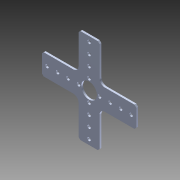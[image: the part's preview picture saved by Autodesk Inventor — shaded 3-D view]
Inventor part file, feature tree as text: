
AUTODESK INVENTOR PART (.ipt)
format: ipt  version: 2014 (Build 180170000, 170)  size: 167,424 bytes
history: native  units: in
note: dims shown in document units (in); Inventor stores cm internally (conversion verified against a paired STEP export)
features: other x2, extrude x1, imported_body x1, sketch x1
ambient origin geometry x8: Origin, YZ Plane, XZ Plane, XY Plane, X Axis, Y Axis, Z Axis, Center Point
bodies: Body1 (feature_tree)
feature tree (5):
  other  "Break-Corner1"
  other  "217-3550-STEP1"
  extrude  "Extrusion1"  Depth=1.0in TaperAngle=0.0deg
  imported_body  "Base1"
  sketch  "Sketch1"  dims[d0=0.75in d1=1.0in d2=0.0in]
